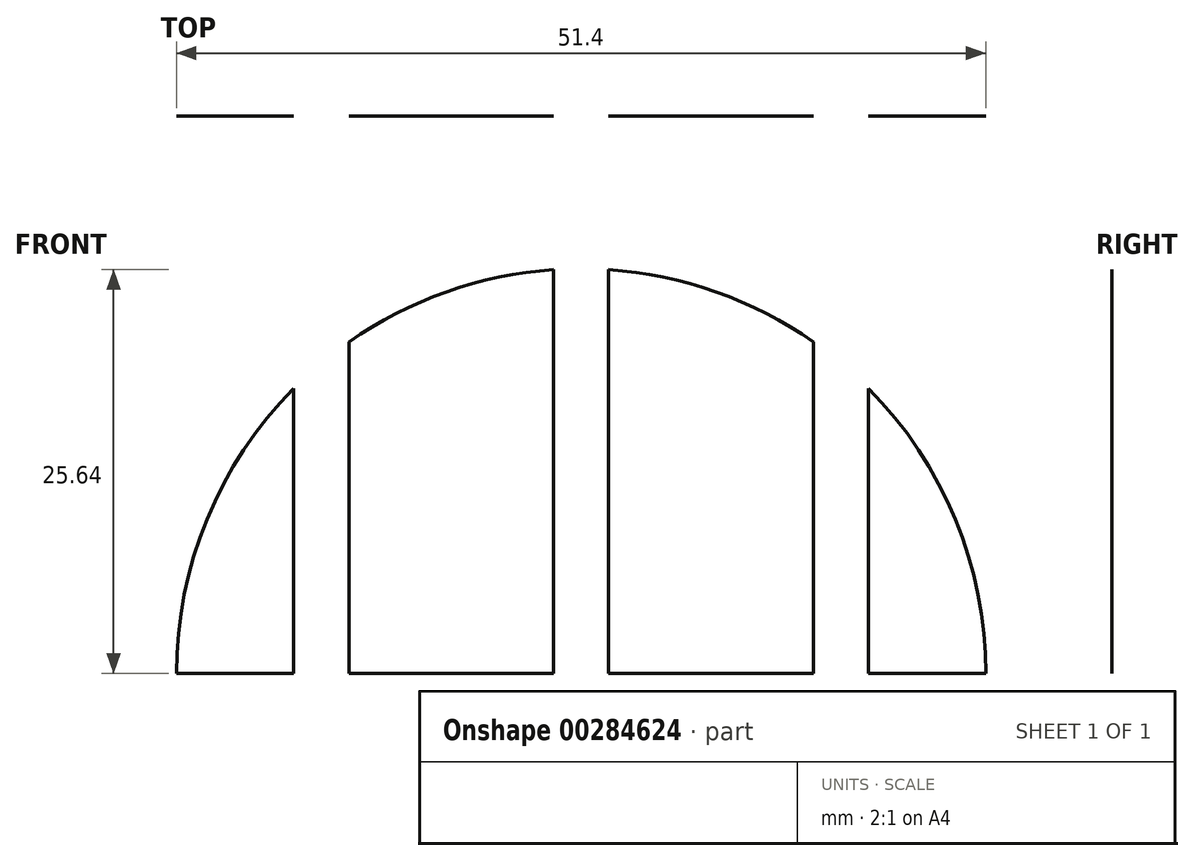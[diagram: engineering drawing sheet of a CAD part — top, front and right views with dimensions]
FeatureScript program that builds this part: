
annotation { "Feature Type Name" : "Feature", "Feature Type Description" : "" }
export const myFeature = defineFeature(function(context is Context, id is Id, definition is map)
    precondition{}
    {
        {
            var Q0;
            Q0=qCreatedBy(makeId("Front.planeOp"),FACE);
            var sketch = newSketch(context, id + "F0", { "sketchPlane" : qUnion([Q0])});
            skCircle(sketch, "E0", {"center": v(0, 0) * mm, "radius": 25.7 * mm});
            skLineSegment(sketch, "E1", {"start": v(-25.7, 0) * mm, "end": v(25.7, 0) * mm});
            skLineSegment(sketch, "E2", {"start": v(0, 25.7) * mm, "end": v(0, -25.7) * mm});
            skLineSegment(sketch, "E3", {"start": v(-1.75, 0) * mm, "end": v(-1.75, 25.64) * mm});
            skLineSegment(sketch, "E4", {"start": v(1.75, 0) * mm, "end": v(1.75, 25.64) * mm});
            skLineSegment(sketch, "E5", {"start": v(-1.75, 12.82) * mm, "end": v(1.75, 12.82) * mm});
            skPoint(sketch, "E6", {"position": v(0, 12.82) * mm});
            skLineSegment(sketch, "E7", {"start": v(-18.25, 18.1) * mm, "end": v(-18.25, 0) * mm});
            skLineSegment(sketch, "E8", {"start": v(-14.75, 21.05) * mm, "end": v(-14.75, 0) * mm});
            skLineSegment(sketch, "E9", {"start": v(14.75, 21.05) * mm, "end": v(14.75, 0) * mm});
            skLineSegment(sketch, "E10", {"start": v(18.25, 18.1) * mm, "end": v(18.25, 0) * mm});
            skSolve(sketch);
        }
        {
            var Q0;
            {var subQ3=sQuery(id+"F0.wireOp",EDGE,"E10");Q0=makeQuery(id+"F0.imprint","IMPRINT",FACE,{"disambiguationData":[TD([[makeQuery(id+"F0.imprint","IMPRINT",EDGE,{"derivedFrom":subQ3}),1.0]])]});}
            var Q1;
            {var subQ3=sQuery(id+"F0.wireOp",EDGE,"E7");Q1=makeQuery(id+"F0.imprint","IMPRINT",FACE,{"disambiguationData":[TD([[makeQuery(id+"F0.imprint","IMPRINT",EDGE,{"derivedFrom":subQ3}),-1.0]])]});}
            var Q2;
            {var subQ4=sQuery(id+"F0.wireOp",EDGE,"E9");Q2=makeQuery(id+"F0.imprint","IMPRINT",FACE,{"disambiguationData":[TD([[makeQuery(id+"F0.imprint","IMPRINT",EDGE,{"derivedFrom":subQ4}),-1.0]])]});}
            var Q3;
            {var subQ6=sQuery(id+"F0.wireOp",EDGE,"E8");Q3=makeQuery(id+"F0.imprint","IMPRINT",FACE,{"disambiguationData":[TD([[makeQuery(id+"F0.imprint","IMPRINT",EDGE,{"derivedFrom":subQ6}),1.0]])]});}
            var Q4;
            {var subQ0=sQuery(id+"F0.wireOp",EDGE,"E1");var subQ4=sQuery(id+"F0.wireOp",EDGE,"E0");var subQ5=makeQuery(id+"F0.imprint","INTERSECT",VERTEX,{"disambiguationData":[OD(0.0)],"derivedFrom":[subQ4,subQ0]});Q4=makeQuery(id+"F0.imprint","IMPRINT",FACE,{"disambiguationData":[TD([[makeQuery(id+"F0.imprint","IMPRINT",EDGE,{"disambiguationData":[TD([[subQ5,-1.0]])],"derivedFrom":subQ4}),1.0]])]});}
            var Q5;
            {var subQ0=sQuery(id+"F0.wireOp",EDGE,"E1");var subQ6=sQuery(id+"F0.wireOp",EDGE,"E0");var subQ7=makeQuery(id+"F0.imprint","INTERSECT",VERTEX,{"disambiguationData":[OD(1.0)],"derivedFrom":[subQ6,subQ0]});Q5=makeQuery(id+"F0.imprint","IMPRINT",FACE,{"disambiguationData":[TD([[makeQuery(id+"F0.imprint","IMPRINT",EDGE,{"disambiguationData":[TD([[subQ7,1.0]])],"derivedFrom":subQ6}),1.0]])]});}
            extrude(context, id + "F1", {"entities" : qUnion([Q0, Q1, Q2, Q3, Q4, Q5]), "depth" : 1 / 203.2 * mm});
        }
    });
